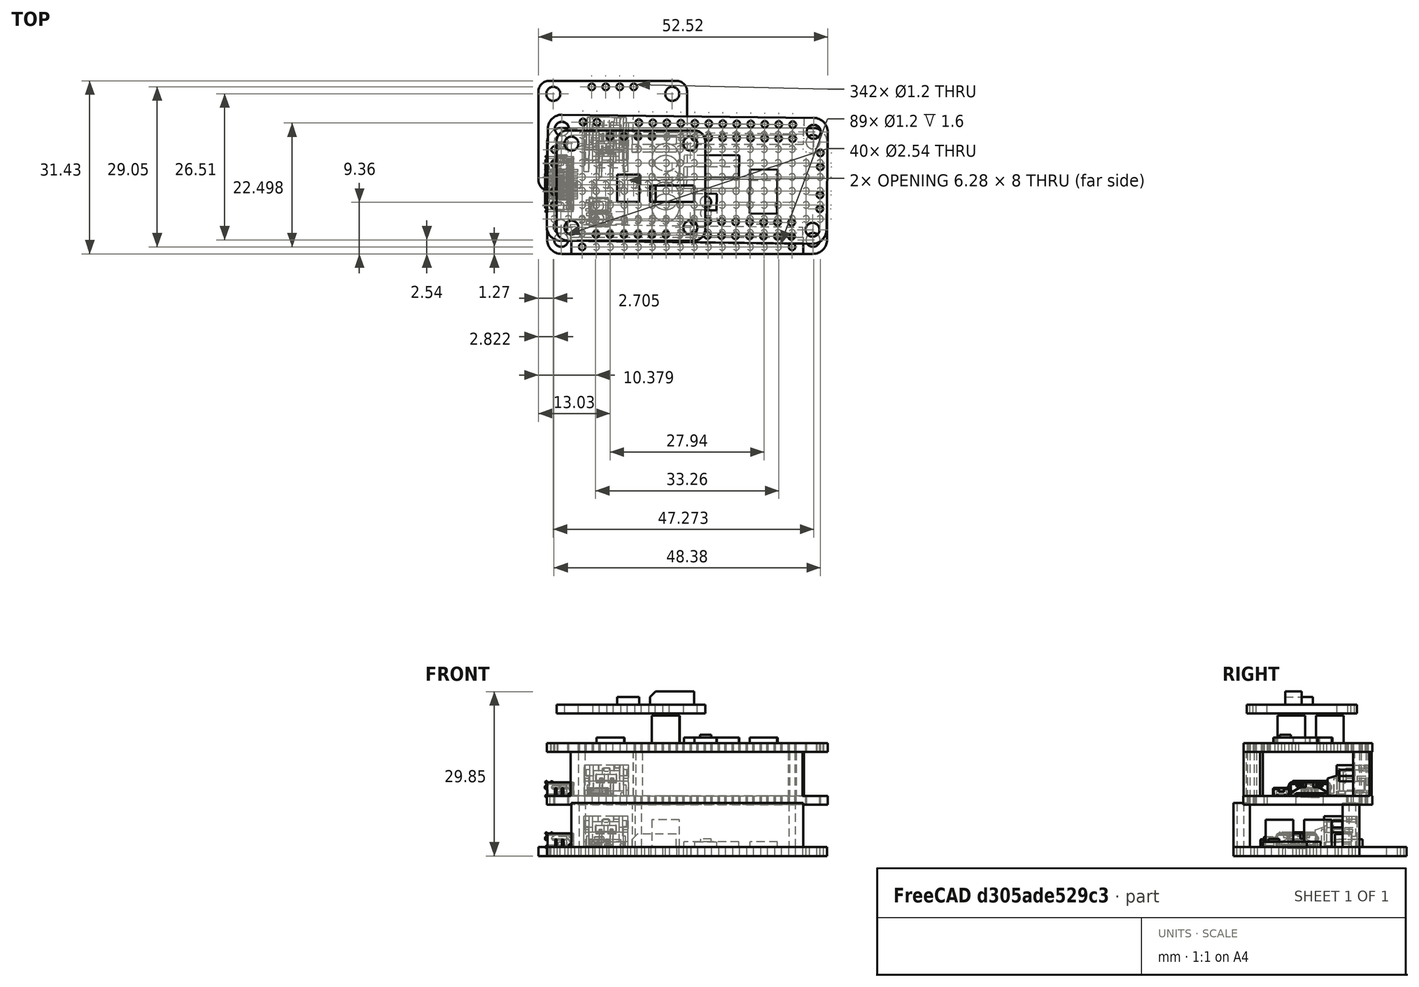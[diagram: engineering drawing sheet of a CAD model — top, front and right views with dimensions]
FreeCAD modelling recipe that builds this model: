
FCSTD DOCUMENT  (FreeCAD 0.16R6706 (Git))
Label: Arduino
License: All rights reserved
LicenseURL: http://en.wikipedia.org/wiki/All_rights_reserved
objects: Part::Feature×32, Sketcher::SketchObject×8, PartDesign::Pad×8, Part::MultiFuse×3, PartDesign::Fillet×1, PartDesign::Chamfer×1, App::DocumentObjectGroup×1
note: 61 computed .brp shape members not serialized (recipe doc carries the construction recipe); baked Part::Feature solids carry a one-line shape summary decoded from their .brp

FEATURE [Part::Feature] Part__Feature077  label="pin"
  Placement = pos=(-14.75,17.5,1.56) rot=(0,0,1;1.5708rad)
  shape: bbox 0.5 x 7.8 x 3.26 mm, 22 faces (baked)
FEATURE [Part::Feature] Part__Feature078  label="mount"
  Placement = pos=(-14.75,17.5,1.56) rot=(0,0,1;1.5708rad)
  shape: bbox 0.5 x 3.4 x 2 mm, 6 faces (baked)
FEATURE [Part::Feature] Part__Feature079  label="housing"
  Placement = pos=(-14.75,17.5,1.56) rot=(0,0,1;1.5708rad)
  shape: bbox 9.006 x 7.908 x 5.712 mm, 118 faces (baked)
FEATURE [Part::Feature] Part__Feature080  label="pin001"
  Placement = pos=(-16.75,17.5,1.56) rot=(0,0,1;1.5708rad)
  shape: bbox 0.5 x 7.8 x 3.26 mm, 22 faces (baked)
FEATURE [Part::Feature] Part__Feature081  label="mount001"
  Placement = pos=(-21.35,17.5,1.56) rot=(0,0,1;1.5708rad)
  shape: bbox 0.5 x 3.4 x 2 mm, 6 faces (baked)
FEATURE [Part::Feature] Part__Feature105  label="smt_tact_button v3"
  Placement = pos=(-16,-5,1.6) rot=(0,0,1;1.5708rad)
  shape: bbox 3.54 x 3 x 1.3 mm, 57 faces (baked)
FEATURE [Part::Feature] Part__Feature106  label="smt_tact_button v004"
  Placement = pos=(-16,-5,1.6) rot=(0,0,1;1.5708rad)
  shape: bbox 1 x 0.5 x 0.15 mm, 6 faces (baked)
FEATURE [Part::Feature] Part__Feature107  label="smt_tact_button v005"
  Placement = pos=(-16,-5,1.6) rot=(0,0,1;1.5708rad)
  shape: bbox 1 x 0.5 x 0.15 mm, 6 faces (baked)
FEATURE [Part::Feature] Part__Feature108  label="smt_tact_button v006"
  Placement = pos=(-16,-5,1.6) rot=(0,0,1;1.5708rad)
  shape: bbox 1 x 0.5 x 0.15 mm, 6 faces (baked)
FEATURE [Part::Feature] Part__Feature109  label="smt_tact_button v007"
  Placement = pos=(-16,-5,1.6) rot=(0,0,1;1.5708rad)
  shape: bbox 1 x 0.5 x 0.15 mm, 6 faces (baked)
FEATURE [Part::Feature] Part__Feature110  label="smt_tact_button v008"
  Placement = pos=(-16,-5,1.6) rot=(0,0,1;1.5708rad)
  shape: bbox 3.69 x 3 x 1.2 mm, 59 faces (baked)
FEATURE [Part::Feature] Part__Feature111  label="smt_tact_button v009"
  Placement = pos=(-16,-5,1.6) rot=(0,0,1;1.5708rad)
  shape: bbox 1.86 x 1.86 x 1.05 mm, 5 faces (baked)
FEATURE [Part::Feature] Part__Feature112  label="Component18"
  Placement = pos=(-22.9662,0.0576377,1.595) rot=(0,0,-1;1.5708rad)
  shape: bbox 4.3 x 0.35 x 1.57 mm, 15 faces (baked)
FEATURE [Part::Feature] Part__Feature113  label="Component19"
  Placement = pos=(-22.9662,0.0676377,1.595) rot=(0,0,-1;1.5708rad)
  shape: bbox 5.13 x 7.98 x 4.195 mm, 243 faces (baked)
FEATURE [Part::Feature] Part__Feature114  label="Component20"
  Placement = pos=(-22.9662,0.0676377,1.595) rot=(0,0,-1;1.5708rad)
  shape: bbox 3.5 x 6.89 x 2.421 mm, 134 faces (baked)
FEATURE [Part::Feature] Part__Feature115  label="Component021"
  Placement = pos=(-22.9662,0.707638,1.595) rot=(0,0,-1;1.5708rad)
  shape: bbox 4.3 x 0.35 x 1.57 mm, 15 faces (baked)
FEATURE [Part::Feature] Part__Feature116  label="Component022"
  Placement = pos=(-22.9662,1.35764,1.595) rot=(0,0,-1;1.5708rad)
  shape: bbox 4.3 x 0.35 x 1.57 mm, 15 faces (baked)
FEATURE [Part::Feature] Part__Feature117  label="Component023"
  Placement = pos=(-22.9662,2.00764,1.595) rot=(0,0,-1;1.5708rad)
  shape: bbox 4.3 x 0.35 x 1.57 mm, 15 faces (baked)
FEATURE [Part::Feature] Part__Feature118  label="Component024"
  Placement = pos=(-22.9662,2.65764,1.595) rot=(0,0,-1;1.5708rad)
  shape: bbox 4.3 x 0.35 x 1.57 mm, 15 faces (baked)
FEATURE [Part::Feature] Part__Feature146  label="smt_led_0805 v2"
  Placement = pos=(-22.7975,5.90247,1.6) rot=(0,0,1;1.5708rad)
  shape: bbox 0.8 x 1.1 x 0.02 mm, 12 faces (baked)
FEATURE [Part::Feature] Part__Feature147  label="smt_led_0805 v003"
  Placement = pos=(-22.7975,5.90247,1.6) rot=(0,0,1;1.5708rad)
  shape: bbox 0.8 x 1.1 x 0.02 mm, 8 faces (baked)
FEATURE [Part::Feature] Part__Feature148  label="smt_led_0805 v004"
  Placement = pos=(-22.7975,5.90247,1.6) rot=(0,0,1;1.5708rad)
  shape: bbox 2 x 1.2 x 0.26 mm, 10 faces (baked)
FEATURE [Part::Feature] Part__Feature149  label="smt_led_0805 v005"
  Placement = pos=(-22.7975,5.90247,1.6) rot=(0,0,1;1.5708rad)
  shape: bbox 0.6 x 1.2 x 0.02 mm, 12 faces (baked)
FEATURE [Part::Feature] Part__Feature150  label="smt_led_0805 v006"
  Placement = pos=(-22.7975,5.90247,1.6) rot=(0,0,1;1.5708rad)
  shape: bbox 0.6 x 1.2 x 0.02 mm, 12 faces (baked)
FEATURE [Part::Feature] Part__Feature151  label="smt_led_0805 v007"
  Placement = pos=(-22.7975,5.90247,1.6) rot=(0,0,1;1.5708rad)
  shape: bbox 1.1 x 1.2 x 0.64 mm, 23 faces (baked)
FEATURE [Part::Feature] Part__Feature152  label="smt_led_0805 v008"
  Placement = pos=(-22.7975,5.90247,1.6) rot=(0,0,1;1.5708rad)
  shape: bbox 0.25 x 0.25 x 0.1 mm, 6 faces (baked)
FEATURE [Part::Feature] Part__Feature  label="board"
  shape: bbox 50.8 x 22.86 x 1.6 mm, 47 faces (baked)
FEATURE [Part::MultiFuse] Fusion  label="Feather"
  Shapes = -> [Part__Feature079,Part__Feature115,Part__Feature148,Part__Feature146,Part__Feature116,Part__Feature118,Part__Feature147,Part__Feature117,Part__Feature149,Part__Feature150,Part__Feature151,Part__Feature152,Part__Feature078,Part__Feature080,Part__Feature077,Part__Feature081,Part__Feature106,Part__Feature111,Part__Feature110,Part__Feature108,Part__Feature113,Part__Feature109,Part__Feature107,+4 more]
FEATURE [Sketcher::SketchObject] Sketch  label="Headers"
  ExternalGeometry = -> [Fusion]
  Placement = pos=(0,0,1.6) rot=(0,0,1;0rad)
  Support = -> Fusion [Face3]
  sketch-geometry (16):
    g0: LineSegment StartX=-21.05 StartY=-8.43 StartZ=0 EndX=21.05 EndY=-8.43 EndZ=0
    g1: LineSegment StartX=21.05 StartY=-8.43 StartZ=0 EndX=21.05 EndY=-11.43 EndZ=0
    g2: LineSegment StartX=21.05 StartY=-11.43 StartZ=0 EndX=-21.05 EndY=-11.43 EndZ=0
    g3: LineSegment StartX=-21.05 StartY=-11.43 StartZ=0 EndX=-21.05 EndY=-8.43 EndZ=0
    g4: LineSegment StartX=-9.89 StartY=11.43 StartZ=0 EndX=21.05 EndY=11.43 EndZ=0
    g5: LineSegment StartX=21.05 StartY=11.43 StartZ=0 EndX=21.05 EndY=8.43 EndZ=0
    g6: LineSegment StartX=21.05 StartY=8.43 StartZ=0 EndX=-9.89 EndY=8.43 EndZ=0
    g7: LineSegment StartX=-9.89 StartY=8.43 StartZ=0 EndX=-9.89 EndY=11.43 EndZ=0
    g8: Circle CenterX=19.05 CenterY=10.16 CenterZ=0 NormalX=0 NormalY=0 NormalZ=1 Radius=0.6
    g9: GeomPoint [constr] X=18.6467 Y=10.6042 Z=0
    g10: Circle CenterX=-8.89 CenterY=10.16 CenterZ=0 NormalX=0 NormalY=0 NormalZ=1 Radius=0.6
    g11: Circle CenterX=19.05 CenterY=-10.16 CenterZ=0 NormalX=0 NormalY=0 NormalZ=1 Radius=0.6
    g12: Circle CenterX=-19.05 CenterY=-10.16 CenterZ=0 NormalX=0 NormalY=0 NormalZ=1 Radius=0.6
    g13: GeomPoint [constr] X=-8.46871 Y=10.5872 Z=0
    g14: GeomPoint [constr] X=-18.7516 Y=-9.63947 Z=0
    g15: GeomPoint [constr] X=19.3891 Y=-9.66503 Z=0
  constraints (36):
    c: Coincident(g0,g1)
    c: Coincident(g1,g2)
    c: Coincident(g2,g3)
    c: Coincident(g3,g0)
    c: Horizontal(g0)
    c: Horizontal(g2)
    c: Vertical(g1)
    c: Vertical(g3)
    c: PointOnObject(g2,g-3)
    c: DistanceX(g0,g-4) = 2
    c: DistanceX(g-5,g0) = 2
    c: DistanceY(g1,g1) = 3
    c: Coincident(g4,g5)
    c: Coincident(g5,g6)
    c: Coincident(g6,g7)
    c: Coincident(g7,g4)
    c: Horizontal(g4)
    c: Horizontal(g6)
    c: Vertical(g5)
    c: Vertical(g7)
    c: PointOnObject(g4,g-7)
    c: DistanceX(g-8,g5) = 2
    c: DistanceX(g6,g-6) = 1
    c: DistanceY(g5,g5) = 3
    c: Coincident(g8,g-8)
    c: PointOnObject(g9,g8)
    c: PointOnObject(g9,g-8)
    c: Coincident(g10,g-6)
    c: Coincident(g11,g-5)
    c: Coincident(g12,g-4)
    c: PointOnObject(g13,g10)
    c: PointOnObject(g13,g-6)
    c: PointOnObject(g14,g12)
    c: PointOnObject(g14,g-4)
    c: PointOnObject(g15,g11)
    c: PointOnObject(g15,g-5)
FEATURE [PartDesign::Pad] Pad  label="Feather+Headers"
  Length = 8
  Length2 = 100
  Sketch = -> Sketch
  Type = 0
FEATURE [Part::Feature] Part__Feature153  label="Board"
  shape: bbox 50.8 x 22.86 x 1.6 mm, 178 faces (baked)
FEATURE [Sketcher::SketchObject] Sketch001  label="Capacitors"
  ExternalGeometry = -> [Part__Feature153]
  Placement = pos=(0,0,1.6) rot=(0,0,1;0rad)
  Support = -> Part__Feature153 [Face177]
  sketch-geometry (3):
    g0: Circle CenterX=-3.9 CenterY=3.93 CenterZ=0 NormalX=0 NormalY=0 NormalZ=1 Radius=2.5
    g1: Circle CenterX=-3.9 CenterY=-3.07 CenterZ=0 NormalX=0 NormalY=0 NormalZ=1 Radius=2.5
    g2: LineSegment [constr] StartX=-3.9 StartY=6.43 StartZ=0 EndX=-3.9 EndY=-5.57 EndZ=0
  constraints (10):
    c: Equal(g0,g1)
    c: PointOnObject(g2,g0)
    c: Vertical(g2)
    c: PointOnObject(g0,g2)
    c: PointOnObject(g1,g2)
    c: DistanceY(g2,g2) = 12
    c: Radius(g0) = 2.5
    c: PointOnObject(g2,g1)
    c: DistanceY(g2,g-3) = 17
    c: DistanceX(g-4,g0) = 21.5
FEATURE [PartDesign::Pad] Pad001  label="Caps"
  Length = 5
  Length2 = 100
  Sketch = -> Sketch001
  Type = 0
FEATURE [Sketcher::SketchObject] Sketch002  label="Chips"
  ExternalGeometry = -> [Pad001]
  Placement = pos=(0,0,1.6) rot=(0,0,1;0rad)
  Support = -> Pad001 [Face2]
  sketch-geometry (16):
    g0: LineSegment StartX=-16.4 StartY=1.93 StartZ=0 EndX=-11.4 EndY=1.93 EndZ=0
    g1: LineSegment StartX=-11.4 StartY=1.93 StartZ=0 EndX=-11.4 EndY=-6.07 EndZ=0
    g2: LineSegment StartX=-11.4 StartY=-6.07 StartZ=0 EndX=-16.4 EndY=-6.07 EndZ=0
    g3: LineSegment StartX=-16.4 StartY=-6.07 StartZ=0 EndX=-16.4 EndY=1.93 EndZ=0
    g4: LineSegment StartX=-0.6 StartY=4.43 StartZ=0 EndX=9.4 EndY=4.43 EndZ=0
    g5: LineSegment StartX=9.4 StartY=4.43 StartZ=0 EndX=9.4 EndY=0.43 EndZ=0
    g6: LineSegment StartX=9.4 StartY=0.43 StartZ=0 EndX=-0.6 EndY=0.43 EndZ=0
    g7: LineSegment StartX=-0.6 StartY=0.43 StartZ=0 EndX=-0.6 EndY=4.43 EndZ=0
    g8: LineSegment StartX=11.4 StartY=1.93 StartZ=0 EndX=16.4 EndY=1.93 EndZ=0
    g9: LineSegment StartX=16.4 StartY=1.93 StartZ=0 EndX=16.4 EndY=-6.07 EndZ=0
    g10: LineSegment StartX=16.4 StartY=-6.07 StartZ=0 EndX=11.4 EndY=-6.07 EndZ=0
    g11: LineSegment StartX=11.4 StartY=-6.07 StartZ=0 EndX=11.4 EndY=1.93 EndZ=0
    g12: LineSegment StartX=1.4 StartY=-2.57 StartZ=0 EndX=5.4 EndY=-2.57 EndZ=0
    g13: LineSegment StartX=5.4 StartY=-2.57 StartZ=0 EndX=5.4 EndY=-5.57 EndZ=0
    g14: LineSegment StartX=5.4 StartY=-5.57 StartZ=0 EndX=1.4 EndY=-5.57 EndZ=0
    g15: LineSegment StartX=1.4 StartY=-5.57 StartZ=0 EndX=1.4 EndY=-2.57 EndZ=0
  constraints (48):
    c: Coincident(g0,g1)
    c: Coincident(g1,g2)
    c: Coincident(g2,g3)
    c: Coincident(g3,g0)
    c: Horizontal(g0)
    c: Horizontal(g2)
    c: Vertical(g1)
    c: Vertical(g3)
    c: Coincident(g4,g5)
    c: Coincident(g5,g6)
    c: Coincident(g6,g7)
    c: Coincident(g7,g4)
    c: Horizontal(g4)
    c: Horizontal(g6)
    c: Vertical(g5)
    c: Vertical(g7)
    c: Coincident(g8,g9)
    c: Coincident(g9,g10)
    c: Coincident(g10,g11)
    c: Coincident(g11,g8)
    c: Horizontal(g8)
    c: Horizontal(g10)
    c: Vertical(g9)
    c: Vertical(g11)
    c: Coincident(g12,g13)
    c: Coincident(g13,g14)
    c: Coincident(g14,g15)
    c: Coincident(g15,g12)
    c: Horizontal(g12)
    c: Horizontal(g14)
    c: Vertical(g13)
    c: Vertical(g15)
    c: DistanceY(g1,g1) = 8
    c: DistanceX(g0,g0) = 5
    c: DistanceX(g8,g8) = 5
    c: DistanceY(g9,g9) = 8
    c: DistanceY(g7,g7) = 4
    c: DistanceX(g4,g4) = 10
    c: DistanceX(g12,g12) = 4
    c: DistanceY(g15,g15) = 3
    c: DistanceX(g8,g-4) = 14
    c: DistanceY(g9,g-3) = 17.5
    c: DistanceY(g6,g-3) = 11
    c: DistanceX(g4,g-4) = 26
    c: DistanceY(g1,g-3) = 17.5
    c: DistanceX(g-5,g0) = 14
    c: DistanceY(g13,g-3) = 17
    c: DistanceX(g14,g-4) = 24
FEATURE [PartDesign::Pad] Pad002  label="Chips001"
  Length = 1
  Length2 = 100
  Sketch = -> Sketch002
  Type = 0
FEATURE [Sketcher::SketchObject] Sketch003  label="Button"
  ExternalGeometry = -> [Pad002]
  Placement = pos=(0,0,2.6) rot=(0,0,1;0rad)
  Support = -> Pad002 [Face206]
  sketch-geometry (4):
    g0: Circle CenterX=3.4 CenterY=-4.07 CenterZ=0 NormalX=0 NormalY=0 NormalZ=1 Radius=1
    g1: LineSegment [constr] StartX=1.4 StartY=-2.57 StartZ=0 EndX=3.4 EndY=-4.07 EndZ=0
    g2: LineSegment [constr] StartX=5.4 StartY=-2.57 StartZ=0 EndX=3.4 EndY=-4.07 EndZ=0
    g3: LineSegment [constr] StartX=1.4 StartY=-5.57 StartZ=0 EndX=3.4 EndY=-4.07 EndZ=0
  constraints (9):
    c: Radius(g0) = 1
    c: Coincident(g1,g-4)
    c: Coincident(g1,g0)
    c: Coincident(g2,g-3)
    c: Coincident(g2,g0)
    c: Coincident(g3,g-4)
    c: Coincident(g3,g0)
    c: Equal(g1,g3)
    c: Equal(g3,g2)
FEATURE [PartDesign::Pad] Pad003
  Length = 0.5
  Length2 = 100
  Sketch = -> Sketch003
  Type = 0
FEATURE [Part::MultiFuse] Fusion001
  Shapes = -> [Part__Feature153,Pad001,Pad002,Pad003]
FEATURE [Sketcher::SketchObject] Sketch004
  Placement = pos=(0,0,0) rot=(1,0,0;3.14159rad)
  Support = -> Fusion001 [Face191]
  sketch-geometry (20):
    g0: LineSegment StartX=-24.9688 StartY=0.835292 StartZ=0 EndX=-23.2769 EndY=0.835292 EndZ=0
    g1: LineSegment StartX=-23.2769 StartY=0.835292 StartZ=0 EndX=-23.2769 EndY=-0.895084 EndZ=0
    g2: LineSegment StartX=-23.2769 StartY=-0.895084 StartZ=0 EndX=-24.9688 EndY=-0.895084 EndZ=0
    g3: LineSegment StartX=-24.9688 StartY=-0.895084 StartZ=0 EndX=-24.9688 EndY=0.835292 EndZ=0
    g4: LineSegment StartX=23.3664 StartY=0.873744 StartZ=0 EndX=24.9814 EndY=0.873744 EndZ=0
    g5: LineSegment StartX=24.9814 StartY=0.873744 StartZ=0 EndX=24.9814 EndY=-0.818178 EndZ=0
    g6: LineSegment StartX=24.9814 StartY=-0.818178 StartZ=0 EndX=23.3664 EndY=-0.818178 EndZ=0
    g7: LineSegment StartX=23.3664 StartY=-0.818178 StartZ=0 EndX=23.3664 EndY=0.873744 EndZ=0
    g8: LineSegment StartX=-20.0468 StartY=-6.70146 StartZ=0 EndX=-15.5863 EndY=-6.70146 EndZ=0
    g9: LineSegment StartX=-15.5863 StartY=-6.70146 StartZ=0 EndX=-15.5863 EndY=-8.47028 EndZ=0
    g10: LineSegment StartX=-15.5863 StartY=-8.47028 StartZ=0 EndX=-20.0468 EndY=-8.47028 EndZ=0
    g11: LineSegment StartX=-20.0468 StartY=-8.47028 StartZ=0 EndX=-20.0468 EndY=-6.70146 EndZ=0
    g12: LineSegment StartX=-14.9326 StartY=-6.663 StartZ=0 EndX=-10.4721 EndY=-6.663 EndZ=0
    g13: LineSegment StartX=-10.4721 StartY=-6.663 StartZ=0 EndX=-10.4721 EndY=-11.0466 EndZ=0
    g14: LineSegment StartX=-10.4721 StartY=-11.0466 StartZ=0 EndX=-14.9326 EndY=-11.0466 EndZ=0
    g15: LineSegment StartX=-14.9326 StartY=-11.0466 StartZ=0 EndX=-14.9326 EndY=-6.663 EndZ=0
    g16: LineSegment StartX=-22.7385 StartY=6.21868 StartZ=0 EndX=22.9049 EndY=6.21868 EndZ=0
    g17: LineSegment StartX=22.9049 StartY=6.21868 StartZ=0 EndX=22.9049 EndY=-6.31693 EndZ=0
    g18: LineSegment StartX=22.9049 StartY=-6.31693 StartZ=0 EndX=-22.7385 EndY=-6.31693 EndZ=0
    g19: LineSegment StartX=-22.7385 StartY=-6.31693 StartZ=0 EndX=-22.7385 EndY=6.21868 EndZ=0
  constraints (40):
    c: Coincident(g0,g1)
    c: Coincident(g1,g2)
    c: Coincident(g2,g3)
    c: Coincident(g3,g0)
    c: Horizontal(g0)
    c: Horizontal(g2)
    c: Vertical(g1)
    c: Vertical(g3)
    c: Coincident(g4,g5)
    c: Coincident(g5,g6)
    c: Coincident(g6,g7)
    c: Coincident(g7,g4)
    c: Horizontal(g4)
    c: Horizontal(g6)
    c: Vertical(g5)
    c: Vertical(g7)
    c: Coincident(g8,g9)
    c: Coincident(g9,g10)
    c: Coincident(g10,g11)
    c: Coincident(g11,g8)
    c: Horizontal(g8)
    c: Horizontal(g10)
    c: Vertical(g9)
    c: Vertical(g11)
    c: Coincident(g12,g13)
    c: Coincident(g13,g14)
    c: Coincident(g14,g15)
    c: Coincident(g15,g12)
    c: Horizontal(g12)
    c: Horizontal(g14)
    c: Vertical(g13)
    c: Vertical(g15)
    c: Coincident(g16,g17)
    c: Coincident(g17,g18)
    c: Coincident(g18,g19)
    c: Coincident(g19,g16)
    c: Horizontal(g16)
    c: Horizontal(g18)
    c: Vertical(g17)
    c: Vertical(g19)
FEATURE [PartDesign::Pad] Pad004
  Length = 1.6
  Length2 = 100
  Reversed = true
  Sketch = -> Sketch004
  Type = 0
FEATURE [Part::Feature] Pad004001  label="Motor Controller"
  Placement = pos=(0.0115062,2.11974,18.8866) rot=(0,0,-1;0.012168rad)
  shape: bbox 51.01 x 23.42 x 6.6 mm, 106 faces (baked)
FEATURE [Part::Feature] Pad004002  label="Feather+Header"
  Placement = pos=(0.00858456,2.10293,9.28662) rot=(0,0,-1;0.011913rad)
  shape: bbox 51.33 x 23.4 x 9.6 mm, 835 faces (baked)
FEATURE [Sketcher::SketchObject] Sketch005
  sketch-geometry (39):
    g0: LineSegment StartX=-27 StartY=20 StartZ=0 EndX=0 EndY=20 EndZ=0
    g1: LineSegment StartX=0 StartY=20 StartZ=0 EndX=0 EndY=0 EndZ=0
    g2: LineSegment StartX=0 StartY=0 StartZ=0 EndX=-27 EndY=0 EndZ=0
    g3: LineSegment StartX=-27 StartY=0 StartZ=0 EndX=-27 EndY=20 EndZ=0
    g4: Circle CenterX=-24.295 CenterY=17.62 CenterZ=0 NormalX=0 NormalY=0 NormalZ=1 Radius=1.27
    g5: Circle CenterX=-24.295 CenterY=2.38 CenterZ=0 NormalX=0 NormalY=0 NormalZ=1 Radius=1.27
    g6: Circle CenterX=-2.705 CenterY=2.38 CenterZ=0 NormalX=0 NormalY=0 NormalZ=1 Radius=1.27
    g7: Circle CenterX=-2.705 CenterY=17.62 CenterZ=0 NormalX=0 NormalY=0 NormalZ=1 Radius=1.27
    g8: LineSegment [constr] StartX=-24.295 StartY=17.62 StartZ=0 EndX=-2.705 EndY=17.62 EndZ=0
    g9: LineSegment [constr] StartX=-2.705 StartY=17.62 StartZ=0 EndX=-2.705 EndY=2.38 EndZ=0
    g10: LineSegment [constr] StartX=-2.705 StartY=2.38 StartZ=0 EndX=-24.295 EndY=2.38 EndZ=0
    g11: LineSegment [constr] StartX=-24.295 StartY=2.38 StartZ=0 EndX=-24.295 EndY=17.62 EndZ=0
    g12: LineSegment [constr] StartX=-27 StartY=20 StartZ=0 EndX=-24.295 EndY=17.62 EndZ=0
    g13: LineSegment [constr] StartX=-2.705 StartY=17.62 StartZ=0 EndX=0 EndY=20 EndZ=0
    g14: LineSegment [constr] StartX=0 StartY=0 StartZ=0 EndX=-2.705 EndY=2.38 EndZ=0
    g15: LineSegment [constr] StartX=-17.31 StartY=18.89 StartZ=0 EndX=-14.77 EndY=18.89 EndZ=0
    g16: LineSegment [constr] StartX=-14.77 StartY=18.89 StartZ=0 EndX=-12.23 EndY=18.89 EndZ=0
    g17: LineSegment [constr] StartX=-12.23 StartY=18.89 StartZ=0 EndX=-9.69 EndY=18.89 EndZ=0
    g18: Circle CenterX=-17.31 CenterY=18.89 CenterZ=0 NormalX=0 NormalY=0 NormalZ=1 Radius=0.6
    g19: Circle CenterX=-14.77 CenterY=18.89 CenterZ=0 NormalX=0 NormalY=0 NormalZ=1 Radius=0.6
    g20: Circle CenterX=-12.23 CenterY=18.89 CenterZ=0 NormalX=0 NormalY=0 NormalZ=1 Radius=0.6
    g21: Circle CenterX=-9.69 CenterY=18.89 CenterZ=0 NormalX=0 NormalY=0 NormalZ=1 Radius=0.6
    g22: LineSegment [constr] StartX=-14.77 StartY=1.11 StartZ=0 EndX=-12.23 EndY=1.11 EndZ=0
    g23: LineSegment [constr] StartX=-12.23 StartY=1.11 StartZ=0 EndX=-9.69 EndY=1.11 EndZ=0
    g24: LineSegment [constr] StartX=-9.69 StartY=1.11 StartZ=0 EndX=-7.15 EndY=1.11 EndZ=0
    g25: Circle CenterX=-14.77 CenterY=1.11 CenterZ=0 NormalX=0 NormalY=0 NormalZ=1 Radius=0.6
    g26: Circle CenterX=-12.23 CenterY=1.11 CenterZ=0 NormalX=0 NormalY=0 NormalZ=1 Radius=0.6
    g27: Circle CenterX=-9.69 CenterY=1.11 CenterZ=0 NormalX=0 NormalY=0 NormalZ=1 Radius=0.6
    g28: Circle CenterX=-7.15 CenterY=1.11 CenterZ=0 NormalX=0 NormalY=0 NormalZ=1 Radius=0.6
    g29: LineSegment [constr] StartX=-19.85 StartY=1.11 StartZ=0 EndX=-17.31 EndY=1.11 EndZ=0
    g30: LineSegment [constr] StartX=-17.31 StartY=1.11 StartZ=0 EndX=-14.77 EndY=1.11 EndZ=0
    g31: Circle CenterX=-19.85 CenterY=1.11 CenterZ=0 NormalX=0 NormalY=0 NormalZ=1 Radius=0.6
    g32: Circle CenterX=-17.31 CenterY=1.11 CenterZ=0 NormalX=0 NormalY=0 NormalZ=1 Radius=0.6
    g33: LineSegment [constr] StartX=-27 StartY=20 StartZ=0 EndX=-17.31 EndY=18.89 EndZ=0
    g34: LineSegment [constr] StartX=-9.69 StartY=18.89 StartZ=0 EndX=0 EndY=20 EndZ=0
    g35: LineSegment [constr] StartX=-7.15 StartY=1.11 StartZ=0 EndX=0 EndY=0 EndZ=0
    g36: LineSegment [constr] StartX=-19.85 StartY=1.11 StartZ=0 EndX=-27 EndY=0 EndZ=0
    g37: LineSegment [constr] StartX=-7.15 StartY=1.11 StartZ=0 EndX=-7.15 EndY=0 EndZ=0
    g38: LineSegment [constr] StartX=-9.69 StartY=18.89 StartZ=0 EndX=-9.69 EndY=20 EndZ=0
  constraints (96):
    c: Coincident(g0,g1)
    c: Coincident(g1,g2)
    c: Coincident(g2,g3)
    c: Coincident(g3,g0)
    c: Horizontal(g0)
    c: Horizontal(g2)
    c: Vertical(g1)
    c: Vertical(g3)
    c: Coincident(g1,g-1)
    c: DistanceX(g0,g0) = 27
    c: DistanceY(g3,g3) = 20
    c: Coincident(g8,g9)
    c: Coincident(g9,g10)
    c: Coincident(g10,g11)
    c: Coincident(g11,g8)
    c: Horizontal(g8)
    c: Horizontal(g10)
    c: Vertical(g9)
    c: Vertical(g11)
    c: Coincident(g8,g4)
    c: Coincident(g9,g6)
    c: Coincident(g7,g8)
    c: Coincident(g5,g10)
    c: Equal(g7,g4)
    c: Equal(g4,g5)
    c: Equal(g5,g6)
    c: DistanceX(g8,g8) = 21.59
    c: DistanceY(g9,g9) = 15.24
    c: Coincident(g12,g0)
    c: Coincident(g12,g4)
    c: Coincident(g13,g7)
    c: Coincident(g13,g0)
    c: Coincident(g14,g6)
    c: Coincident(g14,g-1)
    c: Equal(g13,g14)
    c: Equal(g14,g12)
    c: Radius(g4) = 1.27
    c: Horizontal(g15)
    c: Coincident(g16,g15)
    c: Horizontal(g16)
    c: Coincident(g17,g16)
    c: Horizontal(g17)
    c: Equal(g15,g16)
    c: Equal(g16,g17)
    c: Coincident(g19,g15)
    c: Coincident(g20,g16)
    c: Coincident(g21,g17)
    c: Equal(g21,g20)
    c: Equal(g20,g19)
    c: Equal(g19,g18)
    c: Radius(g21) = 0.6
    c: Coincident(g18,g15)
    c: Horizontal(g22)
    c: Coincident(g23,g22)
    c: Horizontal(g23)
    c: Coincident(g24,g23)
    c: Horizontal(g24)
    c: Equal(g22,g23)
    c: Equal(g23,g24)
    c: Coincident(g26,g22)
    c: Coincident(g27,g23)
    c: Coincident(g28,g24)
    c: Equal(g28,g27)
    c: Equal(g27,g26)
    c: Equal(g26,g25)
    c: Equal(g21,g28) = 0.6
    c: Coincident(g25,g22)
    c: Horizontal(g29)
    c: Coincident(g30,g29)
    c: Horizontal(g30)
    c: Coincident(g32,g29)
    c: Equal(g32,g31)
    c: Coincident(g31,g29)
    c: Coincident(g30,g22)
    c: Equal(g22,g30)
    c: Equal(g30,g29)
    c: Equal(g29,g15)
    c: DistanceY(g29,g15) = 17.78
    c: DistanceX(g15,g15) = 2.54
    c: Coincident(g33,g0)
    c: Coincident(g33,g15)
    c: Coincident(g34,g17)
    c: Coincident(g34,g0)
    c: Coincident(g35,g24)
    c: Coincident(g35,g-1)
    c: Coincident(g36,g29)
    c: Coincident(g36,g2)
    c: Equal(g34,g33)
    c: Equal(g35,g36)
    c: Coincident(g37,g24)
    c: PointOnObject(g37,g2)
    c: Vertical(g37)
    c: PointOnObject(g38,g0)
    c: Vertical(g38)
    c: Equal(g37,g38)
    c: Coincident(g38,g17)
FEATURE [PartDesign::Pad] Pad004003  label="BNO055 board"
  Length = 1.6
  Length2 = 100
  Sketch = -> Sketch005
  Type = 0
FEATURE [PartDesign::Fillet] Fillet  label="BNO055 Fillet"
  Base = -> Pad004003 [Edge8,Edge5,Edge2,Edge1]
  Radius = 2
FEATURE [Sketcher::SketchObject] Sketch006
  ExternalGeometry = -> [Fillet]
  Placement = pos=(0,0,1.6) rot=(0,0,1;0rad)
  Support = -> Fillet [Face5]
  sketch-geometry (4):
    g0: LineSegment StartX=-16 StartY=12 StartZ=0 EndX=-12 EndY=12 EndZ=0
    g1: LineSegment StartX=-12 StartY=12 StartZ=0 EndX=-12 EndY=7 EndZ=0
    g2: LineSegment StartX=-12 StartY=7 StartZ=0 EndX=-16 EndY=7 EndZ=0
    g3: LineSegment StartX=-16 StartY=7 StartZ=0 EndX=-16 EndY=12 EndZ=0
  constraints (12):
    c: Coincident(g0,g1)
    c: Coincident(g1,g2)
    c: Coincident(g2,g3)
    c: Coincident(g3,g0)
    c: Horizontal(g0)
    c: Horizontal(g2)
    c: Vertical(g1)
    c: Vertical(g3)
    c: DistanceX(g0,g0) = 4
    c: DistanceY(g3,g3) = 5
    c: DistanceX(g-3,g1) = 15
    c: DistanceY(g1,g-4) = 13
FEATURE [PartDesign::Pad] Pad004004
  Length = 1.4
  Length2 = 100
  Sketch = -> Sketch006
  Type = 0
FEATURE [Sketcher::SketchObject] Sketch007
  ExternalGeometry = -> [Pad004004]
  Placement = pos=(0,0,1.6) rot=(0,0,1;0rad)
  Support = -> Pad004004 [Face6]
  sketch-geometry (4):
    g0: LineSegment StartX=-10 StartY=10 StartZ=0 EndX=-2 EndY=10 EndZ=0
    g1: LineSegment StartX=-2 StartY=10 StartZ=0 EndX=-2 EndY=7 EndZ=0
    g2: LineSegment StartX=-2 StartY=7 StartZ=0 EndX=-10 EndY=7 EndZ=0
    g3: LineSegment StartX=-10 StartY=7 StartZ=0 EndX=-10 EndY=10 EndZ=0
  constraints (12):
    c: Coincident(g0,g1)
    c: Coincident(g1,g2)
    c: Coincident(g2,g3)
    c: Coincident(g3,g0)
    c: Horizontal(g0)
    c: Horizontal(g2)
    c: Vertical(g1)
    c: Vertical(g3)
    c: DistanceX(g0,g0) = 8
    c: DistanceY(g3,g3) = 3
    c: DistanceY(g1,g-3) = 13
    c: DistanceX(g2,g-4) = 10
FEATURE [PartDesign::Pad] Pad004005
  Length = 2.4
  Length2 = 100
  Sketch = -> Sketch007
  Type = 0
FEATURE [PartDesign::Chamfer] Chamfer  label="BNO055 Chamfer"
  Base = -> Pad004005 [Edge72]
  Size = 1
FEATURE [App::DocumentObjectGroup] Group  label="Parts"
  Group = -> [Fusion001,Pad004,Fusion,Pad,Pad004003,Fillet,Pad004004,Pad004005,Chamfer]
FEATURE [Part::Feature] Chamfer001  label="BNO055"
  Placement = pos=(3.28888,-9.02038,25.8546) rot=(0,0,1;0rad)
  shape: bbox 27 x 20 x 4 mm, 35 faces (baked)
FEATURE [Part::MultiFuse] Fusion002  label="Boards1"
  Shapes = -> [Chamfer001,Pad004002,Pad004001]
FEATURE [Part::Feature] Fusion002001  label="Boards"
  shape: bbox 51.34 x 23.43 x 20.57 mm, 976 faces, 3 solids (baked)
